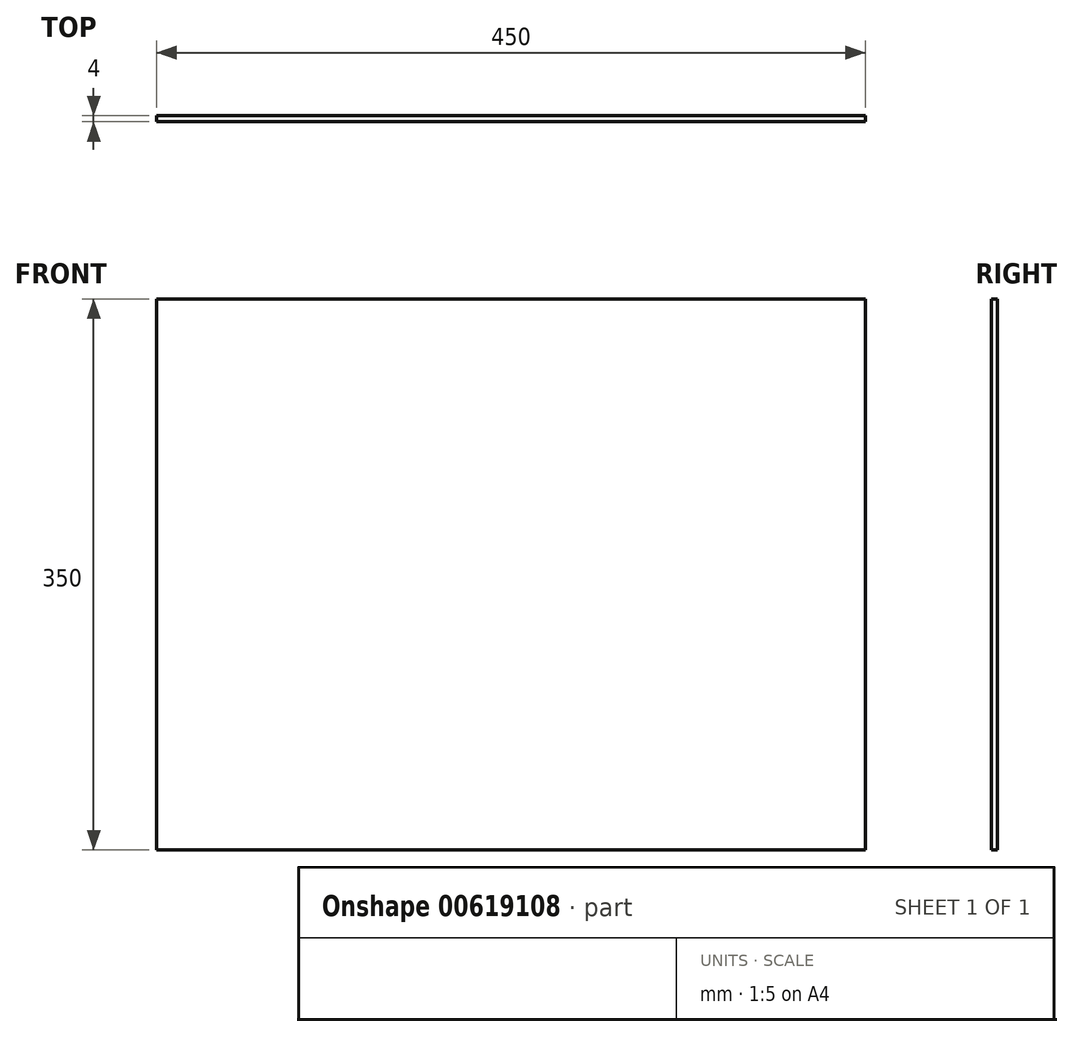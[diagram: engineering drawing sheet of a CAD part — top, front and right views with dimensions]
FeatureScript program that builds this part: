
annotation { "Feature Type Name" : "Feature", "Feature Type Description" : "" }
export const myFeature = defineFeature(function(context is Context, id is Id, definition is map)
    precondition{}
    {
        {
            var Q0;
            Q0=qCreatedBy(makeId("Front.planeOp"),FACE);
            var sketch = newSketch(context, id + "F0", { "sketchPlane" : qUnion([Q0])});
            skLineSegment(sketch, "E0.bottom", {"start": v(225, 175) * mm, "end": v(-225, 175) * mm});
            skLineSegment(sketch, "E0.top", {"start": v(225, -175) * mm, "end": v(-225, -175) * mm});
            skLineSegment(sketch, "E0.left", {"start": v(225, 175) * mm, "end": v(225, -175) * mm});
            skLineSegment(sketch, "E0.right", {"start": v(-225, 175) * mm, "end": v(-225, -175) * mm});
            skPoint(sketch, "E0.middle", {"position": v(0, 0) * mm});
            skSolve(sketch);
        }
        {
            var Q0;
            Q0 = qSketchRegion(id + "F0", true);
            extrude(context, id + "F1", {"entities" : qUnion([Q0]), "depth" : 4 * mm, "offsetDistance" : 25 * mm});
        }
    });
